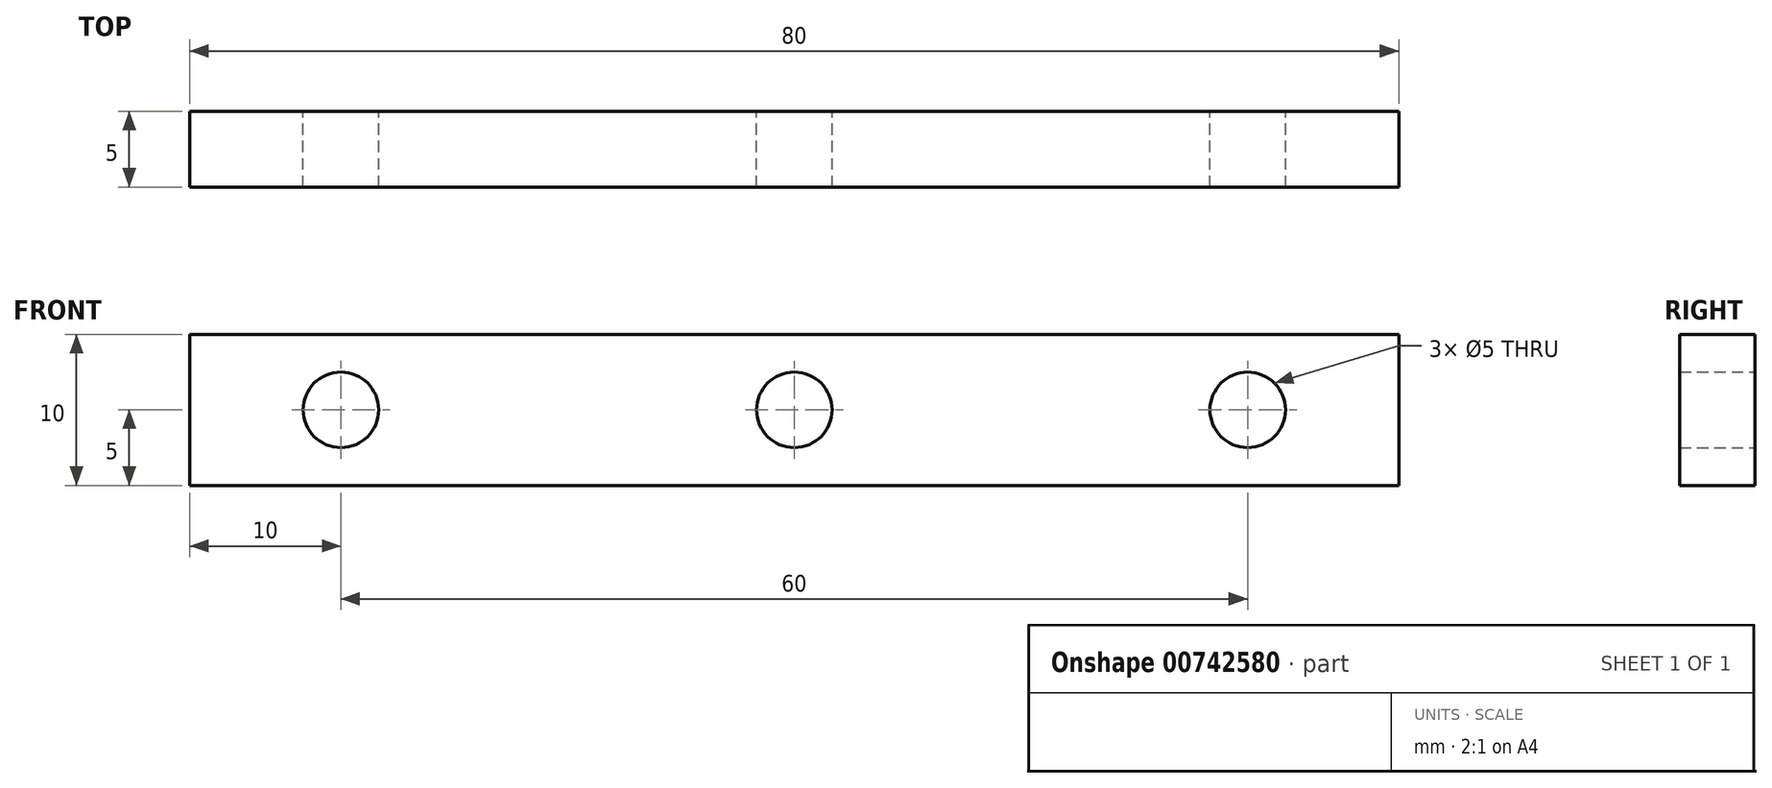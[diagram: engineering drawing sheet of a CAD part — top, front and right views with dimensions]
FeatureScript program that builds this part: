
annotation { "Feature Type Name" : "Feature", "Feature Type Description" : "" }
export const myFeature = defineFeature(function(context is Context, id is Id, definition is map)
    precondition{}
    {
        {
            var Q0;
            Q0=qCreatedBy(makeId("Front.planeOp"),FACE);
            var sketch = newSketch(context, id + "F0", { "sketchPlane" : qUnion([Q0])});
            skLineSegment(sketch, "E0", {"start": v(-31.06, 0) * mm, "end": v(29.98, 0) * mm, "construction": true});
            skCircle(sketch, "E1", {"center": v(-30, 0) * mm, "radius": 2.5 * mm});
            skCircle(sketch, "E2", {"center": v(0, 0) * mm, "radius": 2.5 * mm});
            skCircle(sketch, "E3", {"center": v(30, 0) * mm, "radius": 2.5 * mm});
            skLineSegment(sketch, "E4.bottom", {"start": v(-40, 5) * mm, "end": v(40, 5) * mm});
            skLineSegment(sketch, "E4.top", {"start": v(-40, -5) * mm, "end": v(40, -5) * mm});
            skLineSegment(sketch, "E4.left", {"start": v(-40, 5) * mm, "end": v(-40, -5) * mm});
            skLineSegment(sketch, "E4.right", {"start": v(40, 5) * mm, "end": v(40, -5) * mm});
            skSolve(sketch);
        }
        {
            var Q0;
            Q0=makeQuery(id+"F0.imprint","IMPRINT",FACE,{"disambiguationData":[TD([[makeQuery(id+"F0.imprint","IMPRINT",EDGE,{"derivedFrom":sQuery(id+"F0.wireOp",EDGE,"E1")}),-1.0]])]});
            extrude(context, id + "F1", {"entities" : qUnion([Q0]), "depth" : 5 * mm, "offsetDistance" : 25 * mm});
        }
    });
